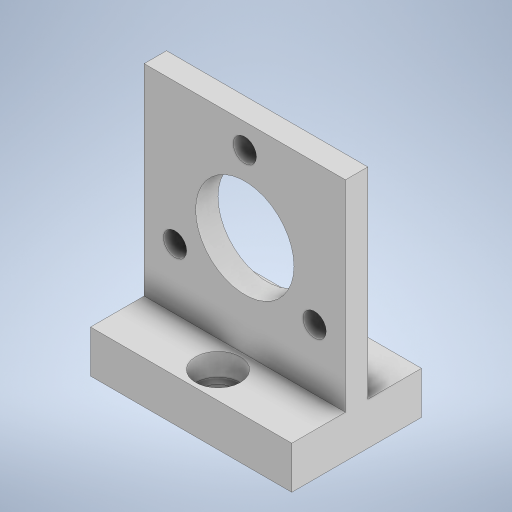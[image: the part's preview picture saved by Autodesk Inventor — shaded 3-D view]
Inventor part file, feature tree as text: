
AUTODESK INVENTOR PART (.ipt)
format: ipt  version: 2024 (Build 280153000, 153)  size: 287,232 bytes
history: native  units: in
note: dims shown in document units (in); Inventor stores cm internally (conversion verified against a paired STEP export)
features: extrude x4, sketch x3
ambient origin geometry x8: Origin, YZ Plane, XZ Plane, XY Plane, X Axis, Y Axis, Z Axis, Center Point
bodies: Body1 (feature_tree)
feature tree (7):
  extrude  "Extrusion2"  Depth=1.7717in
  extrude  "Extrusion9"  Depth=0.6693in
  sketch  "Sketch17"  dims[d4=0.6142in d5=120.0deg d6=0.6142in d7=120.0deg d8=0.2047in d9=0.2047in d10=0.2047in d16=0.1969in d17=0.0in d37=1.2598in d38=0.4724in d39=0.6693in d40=0.0in d41=0.0in d42=0.2441in d43=0.3937in d44=0.2441in d45=0.3937in d46=0.0in d47=0.0in d48=0.1969in d49=0.0in d11=0.0197in d12=0.0344in d13=0.0197in d14=0.0344in d29=0.0197in d30=0.0344in d31=0.0197in d32=0.0344in d33=0.0197in d34=0.0344in d35=0.0344in]
  extrude  "Extrusion10"  TaperAngle=120.0deg  [1 undecoded]
  extrude  "Extrusion11"  Depth=0.1969in
  sketch  "Sketch1"  dims[d0=1.7717in d1=1.7717in]
  sketch  "Sketch16"  dims[d2=0.8661in d3=0.6693in]
note: 1 required parameter value undecoded (feature->parameter linkage not recoverable at this tier; creation-order binding heuristic only, values carry confidence <= 0.55)
